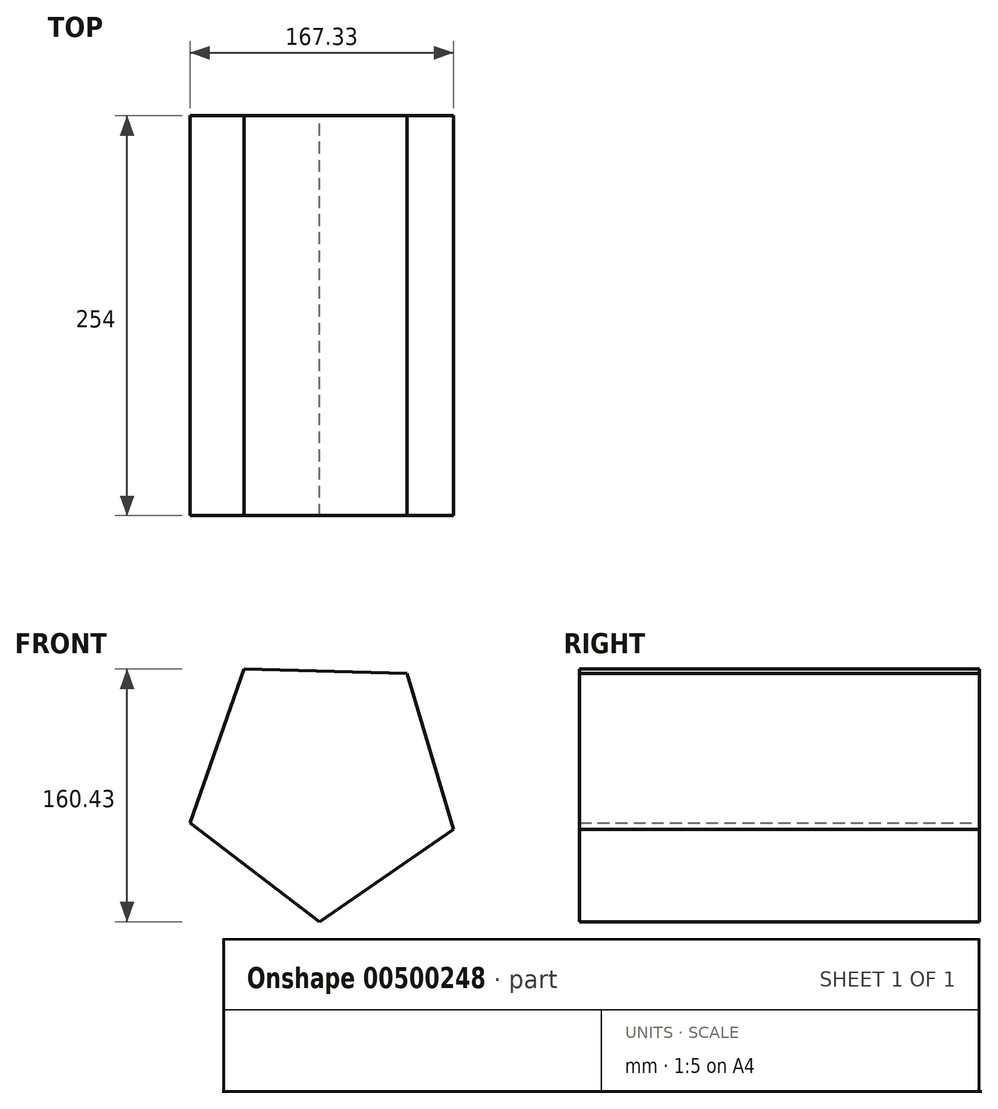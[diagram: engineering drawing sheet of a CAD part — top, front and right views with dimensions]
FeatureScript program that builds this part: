
annotation { "Feature Type Name" : "Feature", "Feature Type Description" : "" }
export const myFeature = defineFeature(function(context is Context, id is Id, definition is map)
    precondition{}
    {
        {
            var Q0;
            Q0=qCreatedBy(makeId("Front.planeOp"),FACE);
            var sketch = newSketch(context, id + "F0", { "sketchPlane" : qUnion([Q0])});
            skCircle(sketch, "E0.cCircle", {"center": v(0, 0) * mm, "radius": 88 * mm, "construction": true});
            skLineSegment(sketch, "E0.0", {"start": v(-84.34, -25.1) * mm, "end": v(-49.94, 72.46) * mm});
            skLineSegment(sketch, "E0.1", {"start": v(-49.94, 72.46) * mm, "end": v(53.48, 69.88) * mm});
            skLineSegment(sketch, "E0.2", {"start": v(53.48, 69.88) * mm, "end": v(83, -29.27) * mm});
            skLineSegment(sketch, "E0.3", {"start": v(83, -29.27) * mm, "end": v(-2.19, -87.97) * mm});
            skLineSegment(sketch, "E0.4", {"start": v(-2.19, -87.97) * mm, "end": v(-84.34, -25.1) * mm});
            skSolve(sketch);
        }
        {
            var Q0;
            Q0=makeQuery(id+"F0.imprint","IMPRINT",FACE,{"disambiguationData":[TD([[makeQuery(id+"F0.imprint","IMPRINT",EDGE,{"derivedFrom":sQuery(id+"F0.wireOp",EDGE,"E0.0")}),-1.0]])]});
            extrude(context, id + "F1", {"entities" : qUnion([Q0]), "depth" : 254 * mm, "offsetDistance" : 25 * mm});
        }
    });
